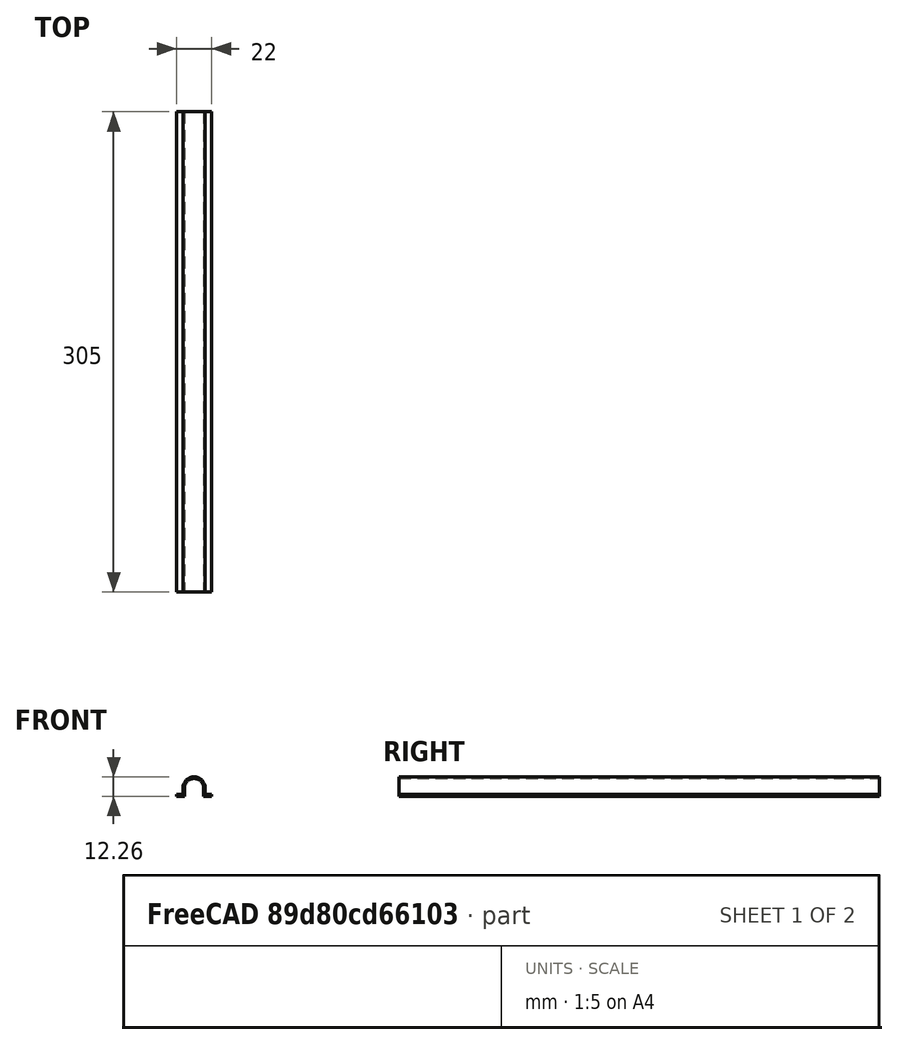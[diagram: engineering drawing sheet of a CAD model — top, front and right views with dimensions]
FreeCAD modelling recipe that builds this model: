
FCSTD DOCUMENT  (FreeCAD 0.21R33771 (Git))
Label: YesTrlrRadioWireCover
License: All rights reserved
LicenseURL: http://en.wikipedia.org/wiki/All_rights_reserved
objects: Sketcher::SketchObject×1, PartDesign::Pad×1, PartDesign::Body×1, App::Part×1
note: 4 computed .brp shape members not serialized (recipe doc carries the construction recipe); baked Part::Feature solids carry a one-line shape summary decoded from their .brp

FEATURE [Sketcher::SketchObject] Sketch
  FullyConstrained = false
  MapMode = 5
  Placement = pos=(0,0,0) rot=(1,0,0;1.5708rad)
  Support = -> [XZ_Plane001]
  sketch-geometry (12):
    g0: ArcOfCircle CenterX=3e-16 CenterY=5.262 CenterZ=0 NormalX=0 NormalY=0 NormalZ=1 AngleXU=0 Radius=6 StartAngle=0 EndAngle=3.14159
    g1: LineSegment StartX=6 StartY=5.262 StartZ=0 EndX=6 EndY=0 EndZ=0
    g2: LineSegment StartX=-6 StartY=-4.1864e-08 StartZ=0 EndX=-6 EndY=5.262 EndZ=0
    g3: ArcOfCircle CenterX=3e-16 CenterY=5.262 CenterZ=0 NormalX=0 NormalY=0 NormalZ=1 AngleXU=0 Radius=7 StartAngle=8.36256e-09 EndAngle=3.14159
    g4: LineSegment StartX=7 StartY=5.262 StartZ=0 EndX=7 EndY=1 EndZ=0
    g5: LineSegment StartX=-11 StartY=0 StartZ=0 EndX=-6 EndY=0 EndZ=0
    g6: LineSegment StartX=11 StartY=0 StartZ=0 EndX=11 EndY=1 EndZ=0
    g7: LineSegment StartX=11 StartY=1 StartZ=0 EndX=7 EndY=1 EndZ=0
    g8: LineSegment StartX=-11 StartY=1 StartZ=0 EndX=-11 EndY=0 EndZ=0
    g9: LineSegment StartX=-7 StartY=1 StartZ=0 EndX=-7 EndY=5.262 EndZ=0
    g10: LineSegment StartX=-7 StartY=1 StartZ=0 EndX=-11 EndY=1 EndZ=0
    g11: LineSegment StartX=6 StartY=0 StartZ=0 EndX=11 EndY=0 EndZ=0
  constraints (38):
    c: Diameter(g0) = 12
    c: Vertical(g1)
    c: Vertical(g2)
    c: PointOnObject(g1,g-1)
    c: DistanceX(g2,g1) = 12
    c: DistanceX(g2,g-1) = 6
    c: DistanceY(g-1,g0) = 5.262
    c: DistanceY(g2,g2) = 5.262
    c: DistanceY(g1,g1) = 5.262
    c: Coincident(g0,g2)
    c: Coincident(g0,g1)
    c: Coincident(g3,g0)
    c: Diameter(g3) = 14
    c: Vertical(g4)
    c: DistanceX(g9,g4) = 14
    c: Coincident(g3,g9)
    c: Coincident(g3,g4)
    c: Coincident(g11,g6)
    c: Coincident(g6,g7)
    c: Coincident(g10,g8)
    c: Coincident(g8,g5)
    c: Horizontal(g5)
    c: Horizontal(g7)
    c: Vertical(g6)
    c: Vertical(g8)
    c: PointOnObject(g5,g-1)
    c: DistanceX(g10,g7) = 22
    c: DistanceX(g10,g-1) = 11
    c: DistanceY(g6,g6) = 1
    c: Coincident(g10,g9)
    c: Coincident(g4,g7)
    c: PointOnObject(g5,g2)
    c: PointOnObject(g11,g1)
    c: DistanceY(g8,g8) = 1
    c: DistanceY(g1,g6) = 0
    c: DistanceX(g7,g7) = 4
    c: DistanceX(g10,g10) = 4
    c: DistanceY(g9,g9) = 4.262
FEATURE [PartDesign::Pad] Pad  label="BodyPad"
  Direction = (0,-1,2e-16)
  Length = 305
  Length2 = 10
  Placement = pos=(0,0,0) rot=(1,0,0;1.5708rad)
  Profile = -> Sketch
  ReferenceAxis = -> Sketch [N_Axis]
  Type = 0
FEATURE [PartDesign::Body] Body  label="CoverBody"
  Group = -> [Sketch,Pad]
  Origin = -> Origin001
  Tip = -> Pad
FEATURE [App::Part] Part  label="CoverPart"
  Group = -> [Body]
  Origin = -> Origin
